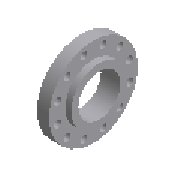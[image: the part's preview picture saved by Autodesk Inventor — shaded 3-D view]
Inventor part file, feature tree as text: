
AUTODESK INVENTOR PART (.ipt)
format: ipt  version: 2023.1 (Build 271208000, 208)  size: 187,904 bytes
history: native  units: mm (DEFAULTED — no unit token found)
features: other x5, sketch x2, revolve x1
ambient origin geometry x8: Origin, YZ Plane, XZ Plane, XY Plane, X Axis, Y Axis, Z Axis, Center Point
bodies: Solid1 (feature_tree)
feature tree (8):
  sketch  "Sketch1"  dims[d11=90.0deg d0=157.5mm]
  revolve  "Revolution1"  [1 undecoded]
  other  "Work Axis1"
  other  "Work Point1"
  other  "Work Point2"
  other  "Work Axis2"
  other  "Work Point3"
  sketch  "Sketch2"  dims[d1=290.0mm d2=159.0mm d3=7.0mm d4=44.5mm d5=0.0mm d6=80.0mm d7=360.0deg d8=70.0mm d9=116.0mm d10=44.5mm d12=32.5mm d13=235.0mm d14=22.5deg]
note: 1 required parameter value undecoded (feature->parameter linkage not recoverable at this tier; creation-order binding heuristic only, values carry confidence <= 0.55)
